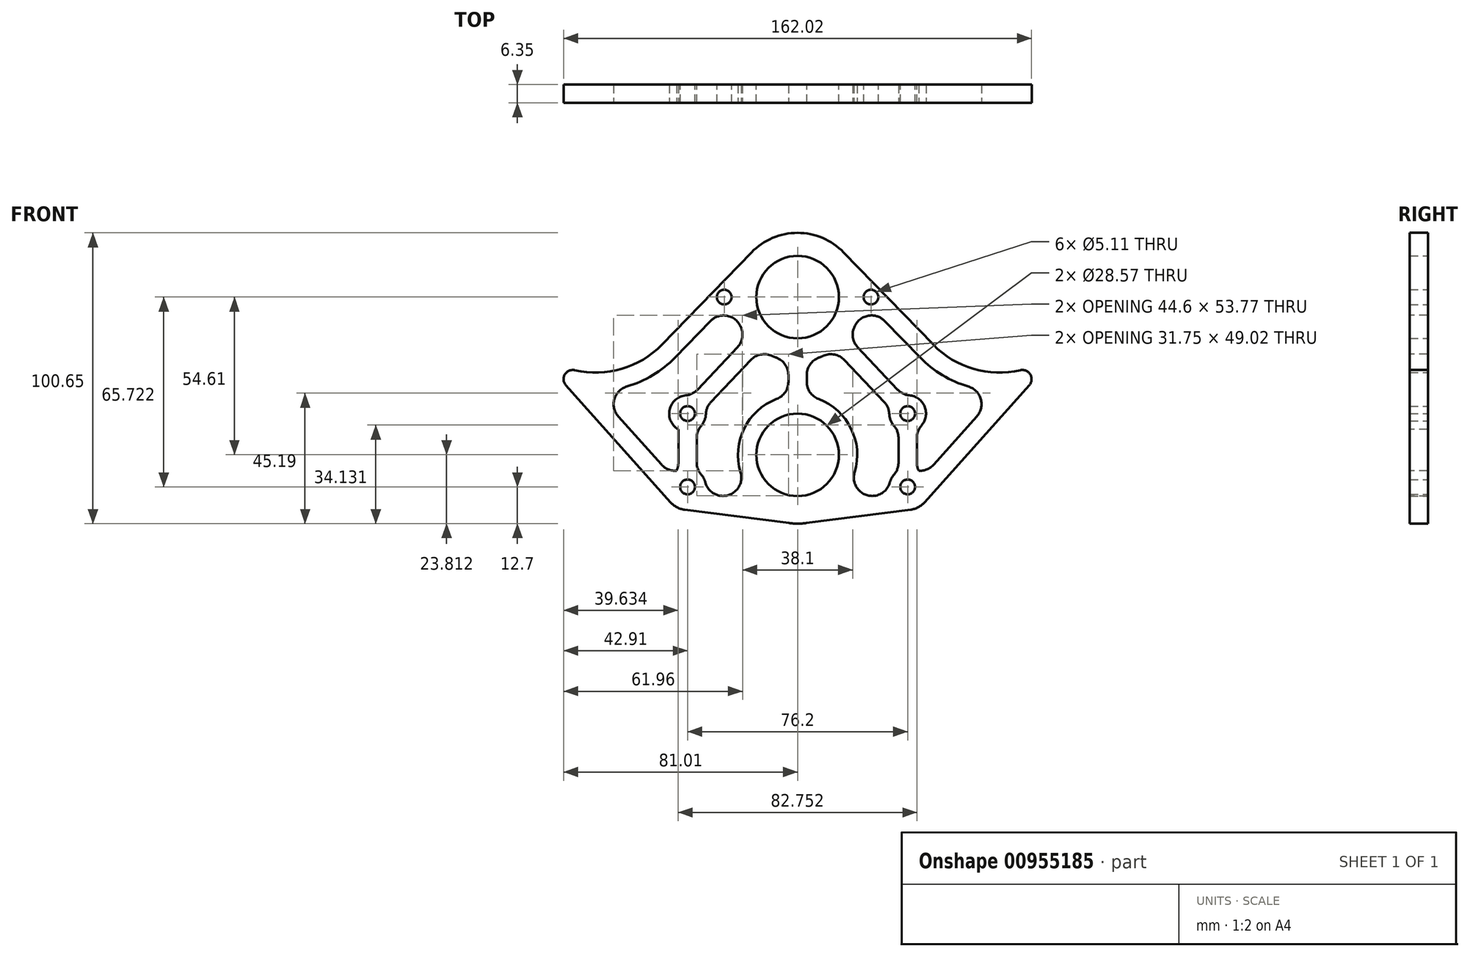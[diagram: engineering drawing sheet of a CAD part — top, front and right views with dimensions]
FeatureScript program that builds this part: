
annotation { "Feature Type Name" : "Feature", "Feature Type Description" : "" }
export const myFeature = defineFeature(function(context is Context, id is Id, definition is map)
    precondition{}
    {
        {
            var Q0;
            Q0=qCreatedBy(makeId("Front.planeOp"),FACE);
            var sketch = newSketch(context, id + "F0", { "sketchPlane" : qUnion([Q0])});
            skCircle(sketch, "E0", {"center": v(-69.85, 58.74) * mm, "radius": 31.88 * mm, "construction": true});
            skCircle(sketch, "E1", {"center": v(69.85, 58.74) * mm, "radius": 31.88 * mm, "construction": true});
            skLineSegment(sketch, "E2", {"start": v(-69.85, 58.74) * mm, "end": v(69.85, 58.74) * mm, "construction": true});
            skLineSegment(sketch, "E3", {"start": v(0, 58.74) * mm, "end": v(0, 0) * mm, "construction": true});
            skLineSegment(sketch, "E4.bottom", {"start": v(-101.6, -25.4) * mm, "end": v(101.6, -25.4) * mm, "construction": true});
            skLineSegment(sketch, "E4.top", {"start": v(-101.6, 25.4) * mm, "end": v(101.6, 25.4) * mm, "construction": true});
            skLineSegment(sketch, "E4.left", {"start": v(-101.6, -25.4) * mm, "end": v(-101.6, 25.4) * mm, "construction": true});
            skLineSegment(sketch, "E4.right", {"start": v(101.6, -25.4) * mm, "end": v(101.6, 25.4) * mm, "construction": true});
            skPoint(sketch, "E4.middle", {"position": v(0, 0) * mm});
            skCircle(sketch, "E5", {"center": v(0, -1.59) * mm, "radius": 50.8 * mm, "construction": true});
            skCircle(sketch, "E6", {"center": v(-69.85, 58.74) * mm, "radius": 7.62 * mm, "construction": true});
            skCircle(sketch, "E7", {"center": v(69.85, 58.74) * mm, "radius": 7.62 * mm, "construction": true});
            skCircle(sketch, "E8", {"center": v(0, 53.02) * mm, "radius": 38.1 * mm, "construction": true});
            skCircle(sketch, "E9", {"center": v(0, 53.02) * mm, "radius": 27.94 * mm, "construction": true});
            skCircle(sketch, "E10", {"center": v(0, -1.59) * mm, "radius": 26.67 * mm, "construction": true});
            skCircle(sketch, "E11", {"center": v(0, 53.02) * mm, "radius": 19.05 * mm, "construction": true});
            skCircle(sketch, "E12", {"center": v(0, -1.59) * mm, "radius": 35.56 * mm, "construction": true});
            skCircle(sketch, "E13", {"center": v(-69.85, 58.74) * mm, "radius": 8.9 * mm, "construction": true});
            skCircle(sketch, "E14", {"center": v(69.85, 58.74) * mm, "radius": 8.9 * mm, "construction": true});
            skCircle(sketch, "E15", {"center": v(0, 53.02) * mm, "radius": 14.29 * mm});
            skCircle(sketch, "E16", {"center": v(0, -1.59) * mm, "radius": 14.29 * mm});
            skCircle(sketch, "E17", {"center": v(-88.9, 12.7) * mm, "radius": 2.55 * mm, "construction": true});
            skCircle(sketch, "E18.0.1.0", {"center": v(-88.9, -12.7) * mm, "radius": 2.55 * mm, "construction": true});
            skCircle(sketch, "E18.1.0.0", {"center": v(-63.5, 12.7) * mm, "radius": 2.55 * mm, "construction": true});
            skCircle(sketch, "E18.1.1.0", {"center": v(-63.5, -12.7) * mm, "radius": 2.55 * mm, "construction": true});
            skCircle(sketch, "E18.2.0.0", {"center": v(-38.1, 12.7) * mm, "radius": 2.55 * mm});
            skCircle(sketch, "E18.2.1.0", {"center": v(-38.1, -12.7) * mm, "radius": 2.55 * mm});
            skCircle(sketch, "E18.3.0.0", {"center": v(-12.7, 12.7) * mm, "radius": 2.55 * mm, "construction": true});
            skCircle(sketch, "E18.3.1.0", {"center": v(-12.7, -12.7) * mm, "radius": 2.55 * mm, "construction": true});
            skCircle(sketch, "E18.4.0.0", {"center": v(12.7, 12.7) * mm, "radius": 2.55 * mm, "construction": true});
            skCircle(sketch, "E18.4.1.0", {"center": v(12.7, -12.7) * mm, "radius": 2.55 * mm, "construction": true});
            skCircle(sketch, "E18.5.0.0", {"center": v(38.1, 12.7) * mm, "radius": 2.55 * mm});
            skCircle(sketch, "E18.5.1.0", {"center": v(38.1, -12.7) * mm, "radius": 2.55 * mm});
            skCircle(sketch, "E18.6.0.0", {"center": v(63.5, 12.7) * mm, "radius": 2.55 * mm, "construction": true});
            skCircle(sketch, "E18.6.1.0", {"center": v(63.5, -12.7) * mm, "radius": 2.55 * mm, "construction": true});
            skCircle(sketch, "E18.7.0.0", {"center": v(88.9, 12.7) * mm, "radius": 2.55 * mm, "construction": true});
            skCircle(sketch, "E18.7.1.0", {"center": v(88.9, -12.7) * mm, "radius": 2.55 * mm, "construction": true});
            skLineSegment(sketch, "E18.direction1", {"start": v(-88.9, 12.7) * mm, "end": v(-63.5, 12.7) * mm, "construction": true});
            skLineSegment(sketch, "E18.direction2", {"start": v(-88.9, 12.7) * mm, "end": v(-88.9, -12.7) * mm, "construction": true});
            skArc(sketch, "E19", {"start": v(-93.62, 37.5) * mm, "mid": v(-98.95, 71.76) * mm, "end": v(-69.85, 90.61) * mm, "construction": true});
            skLineSegment(sketch, "E20", {"start": v(-69.85, 90.61) * mm, "end": v(69.85, 90.61) * mm, "construction": true});
            skArc(sketch, "E21", {"start": v(69.85, 90.61) * mm, "mid": v(98.95, 71.76) * mm, "end": v(93.62, 37.5) * mm, "construction": true});
            skCircle(sketch, "E22", {"center": v(-69.85, 58.74) * mm, "radius": 9.55 * mm, "construction": true});
            skCircle(sketch, "E23", {"center": v(69.85, 58.74) * mm, "radius": 9.55 * mm, "construction": true});
            skLineSegment(sketch, "E24", {"start": v(-67.64, 84.04) * mm, "end": v(-69.85, 58.74) * mm, "construction": true});
            skLineSegment(sketch, "E25", {"start": v(-69.85, 58.74) * mm, "end": v(-72.06, 33.43) * mm, "construction": true});
            skCircle(sketch, "E26", {"center": v(-72.06, 33.43) * mm, "radius": 2.55 * mm, "construction": true});
            skCircle(sketch, "E27", {"center": v(-67.64, 84.04) * mm, "radius": 2.55 * mm, "construction": true});
            skCircle(sketch, "E28.MirrorC", {"center": v(72.06, 33.43) * mm, "radius": 2.55 * mm, "construction": true});
            skLineSegment(sketch, "E29.MirrorCS", {"start": v(69.85, 58.74) * mm, "end": v(72.06, 33.43) * mm, "construction": true});
            skLineSegment(sketch, "E30.MirrorCS", {"start": v(67.64, 84.04) * mm, "end": v(69.85, 58.74) * mm, "construction": true});
            skCircle(sketch, "E31.MirrorC", {"center": v(67.64, 84.04) * mm, "radius": 2.55 * mm, "construction": true});
            skCircle(sketch, "E32", {"center": v(0, -1.59) * mm, "radius": 23.81 * mm, "construction": true});
            skArc(sketch, "E33", {"start": v(3.03, -25.2) * mm, "mid": v(0, -25.4) * mm, "end": v(-3.03, -25.2) * mm});
            skCircle(sketch, "E34", {"center": v(-38.1, -12.7) * mm, "radius": 7.94 * mm, "construction": true});
            skCircle(sketch, "E35", {"center": v(38.1, -12.7) * mm, "radius": 7.94 * mm, "construction": true});
            skLineSegment(sketch, "E36", {"start": v(-3.03, -25.2) * mm, "end": v(-39.11, -20.57) * mm});
            skArc(sketch, "E37", {"start": v(-39.11, -20.57) * mm, "mid": v(-41.8, -19.72) * mm, "end": v(-44.02, -18) * mm});
            skLineSegment(sketch, "E38", {"start": v(-44.02, -18) * mm, "end": v(-80.2, 22.5) * mm});
            skLineSegment(sketch, "E39", {"start": v(3.03, -25.2) * mm, "end": v(39.11, -20.57) * mm});
            skArc(sketch, "E40", {"start": v(39.11, -20.57) * mm, "mid": v(41.8, -19.72) * mm, "end": v(44.02, -18) * mm});
            skLineSegment(sketch, "E41", {"start": v(44.02, -18) * mm, "end": v(80.2, 22.5) * mm});
            skCircle(sketch, "E42", {"center": v(-51.03, 75.8) * mm, "radius": 17.78 * mm, "construction": true});
            skCircle(sketch, "E43", {"center": v(-53.69, 37.52) * mm, "radius": 17.78 * mm, "construction": true});
            skCircle(sketch, "E44", {"center": v(51.03, 75.8) * mm, "radius": 17.78 * mm, "construction": true});
            skCircle(sketch, "E45", {"center": v(53.69, 37.52) * mm, "radius": 17.78 * mm, "construction": true});
            skCircle(sketch, "E46", {"center": v(-51.03, 75.8) * mm, "radius": 11.11 * mm, "construction": true});
            skCircle(sketch, "E47", {"center": v(-53.69, 37.52) * mm, "radius": 11.11 * mm, "construction": true});
            skCircle(sketch, "E48", {"center": v(53.69, 37.52) * mm, "radius": 11.11 * mm, "construction": true});
            skCircle(sketch, "E49", {"center": v(51.03, 75.8) * mm, "radius": 11.11 * mm, "construction": true});
            skCircle(sketch, "E50", {"center": v(0, 53.02) * mm, "radius": 22.23 * mm, "construction": true});
            skArc(sketch, "E51", {"start": v(-77.12, 27.7) * mm, "mid": v(-60.88, 28.15) * mm, "end": v(-46.98, 36.54) * mm});
            skLineSegment(sketch, "E52", {"start": v(-46.98, 36.54) * mm, "end": v(-15.95, 68.5) * mm});
            skArc(sketch, "E53", {"start": v(15.95, 68.5) * mm, "mid": v(0, 75.25) * mm, "end": v(-15.95, 68.5) * mm});
            skArc(sketch, "E54", {"start": v(46.98, 36.54) * mm, "mid": v(60.88, 28.15) * mm, "end": v(77.12, 27.7) * mm});
            skLineSegment(sketch, "E55", {"start": v(46.98, 36.54) * mm, "end": v(15.95, 68.5) * mm});
            skPoint(sketch, "E56.visualSharp", {"position": v(-93.62, 37.5) * mm});
            skArc(sketch, "E56.filletArc", {"start": v(-77.12, 27.7) * mm, "mid": v(-80.57, 26.23) * mm, "end": v(-80.2, 22.5) * mm});
            skPoint(sketch, "E57.visualSharp", {"position": v(93.62, 37.5) * mm});
            skArc(sketch, "E57.filletArc", {"start": v(80.2, 22.5) * mm, "mid": v(80.57, 26.23) * mm, "end": v(77.12, 27.7) * mm});
            skLineSegment(sketch, "E58", {"start": v(25.4, 53.02) * mm, "end": v(0, 53.02) * mm, "construction": true});
            skLineSegment(sketch, "E59", {"start": v(0, 53.02) * mm, "end": v(-25.4, 53.02) * mm, "construction": true});
            skCircle(sketch, "E60", {"center": v(-25.4, 53.02) * mm, "radius": 2.55 * mm});
            skCircle(sketch, "E61", {"center": v(25.4, 53.02) * mm, "radius": 2.55 * mm});
            skSolve(sketch);
        }
        {
            var Q0;
            Q0=qSketchRegion(id+"F0",true);
            extrude(context, id + "F1", {"entities" : qUnion([Q0]), "depth" : 6.35 * mm, "offsetDistance" : 25.4 * mm});
        }
        {
            var Q0;
            Q0=makeQuery(id+"F1.opExtrude","CAP_FACE",FACE,{"disambiguationData":[OSD([sQuery(id+"F0.wireOp",EDGE,"E15"),sQuery(id+"F0.wireOp",EDGE,"E16"),sQuery(id+"F0.wireOp",EDGE,"E18.2.0.0"),sQuery(id+"F0.wireOp",EDGE,"E18.2.1.0"),sQuery(id+"F0.wireOp",EDGE,"E18.5.0.0"),sQuery(id+"F0.wireOp",EDGE,"E18.5.1.0"),sQuery(id+"F0.wireOp",EDGE,"E33"),sQuery(id+"F0.wireOp",EDGE,"E36"),sQuery(id+"F0.wireOp",EDGE,"E37"),sQuery(id+"F0.wireOp",EDGE,"E38"),sQuery(id+"F0.wireOp",EDGE,"E39"),sQuery(id+"F0.wireOp",EDGE,"E40"),sQuery(id+"F0.wireOp",EDGE,"E41"),sQuery(id+"F0.wireOp",EDGE,"E51"),sQuery(id+"F0.wireOp",EDGE,"E52"),sQuery(id+"F0.wireOp",EDGE,"E53"),sQuery(id+"F0.wireOp",EDGE,"E54"),sQuery(id+"F0.wireOp",EDGE,"E55"),sQuery(id+"F0.wireOp",EDGE,"E56.filletArc"),sQuery(id+"F0.wireOp",EDGE,"E57.filletArc"),sQuery(id+"F0.wireOp",EDGE,"E60"),sQuery(id+"F0.wireOp",EDGE,"E61")])],"isStart":false});
            var sketch = newSketch(context, id + "F2", { "sketchPlane" : qUnion([Q0])});
            skCircle(sketch, "E62", {"center": v(0, 53.02) * mm, "radius": 22.23 * mm, "construction": true});
            skCircle(sketch, "E63", {"center": v(25.4, 53.02) * mm, "radius": 6.35 * mm, "construction": true});
            skCircle(sketch, "E64", {"center": v(-25.4, 53.02) * mm, "radius": 6.35 * mm, "construction": true});
            skCircle(sketch, "E65", {"center": v(-38.1, 12.7) * mm, "radius": 6.35 * mm, "construction": true});
            skCircle(sketch, "E66", {"center": v(-38.1, -12.7) * mm, "radius": 6.35 * mm, "construction": true});
            skCircle(sketch, "E67", {"center": v(38.1, -12.7) * mm, "radius": 6.35 * mm, "construction": true});
            skCircle(sketch, "E68", {"center": v(38.1, 12.7) * mm, "radius": 6.35 * mm, "construction": true});
            skLineSegment(sketch, "E69", {"start": v(-38.1, -12.7) * mm, "end": v(-38.1, 12.7) * mm, "construction": true});
            skLineSegment(sketch, "E70", {"start": v(-41.27, -7.2) * mm, "end": v(-41.27, 7.2) * mm});
            skLineSegment(sketch, "E71", {"start": v(-34.92, -7.2) * mm, "end": v(-34.92, 7.2) * mm});
            skCircle(sketch, "E72", {"center": v(0, -1.59) * mm, "radius": 20.64 * mm, "construction": true});
            skLineSegment(sketch, "E73", {"start": v(0, -1.59) * mm, "end": v(0, 53.02) * mm, "construction": true});
            skLineSegment(sketch, "E74", {"start": v(-3.18, 18.8) * mm, "end": v(-3.18, 31.03) * mm});
            skLineSegment(sketch, "E75", {"start": v(0, 53.02) * mm, "end": v(-38.1, 12.7) * mm, "construction": true});
            skLineSegment(sketch, "E76", {"start": v(-32.02, 14.52) * mm, "end": v(-12.8, 34.85) * mm});
            skArc(sketch, "E77.0", {"start": v(-38.3, -14.27) * mm, "mid": v(-38.84, -14.1) * mm, "end": v(-39.28, -13.76) * mm, "construction": true});
            skLineSegment(sketch, "E77.1", {"start": v(42.42, 32.11) * mm, "end": v(11.4, 64.08) * mm, "construction": true});
            skArc(sketch, "E77.2", {"start": v(11.4, 64.08) * mm, "mid": v(0, 68.9) * mm, "end": v(-11.4, 64.08) * mm, "construction": true});
            skLineSegment(sketch, "E77.3", {"start": v(-42.42, 32.11) * mm, "end": v(-11.4, 64.08) * mm, "construction": true});
            skArc(sketch, "E77.4", {"start": v(-69.92, 20.51) * mm, "mid": v(-54.99, 23.52) * mm, "end": v(-42.42, 32.11) * mm});
            skArc(sketch, "E77.5", {"start": v(42.42, 32.11) * mm, "mid": v(54.99, 23.52) * mm, "end": v(69.92, 20.51) * mm, "construction": true});
            skLineSegment(sketch, "E77.6", {"start": v(-39.28, -13.76) * mm, "end": v(-69.92, 20.51) * mm, "construction": true});
            skLineSegment(sketch, "E77.7", {"start": v(39.28, -13.76) * mm, "end": v(69.92, 20.51) * mm, "construction": true});
            skArc(sketch, "E77.8", {"start": v(38.3, -14.27) * mm, "mid": v(38.84, -14.1) * mm, "end": v(39.28, -13.76) * mm, "construction": true});
            skLineSegment(sketch, "E77.9", {"start": v(2.22, -18.9) * mm, "end": v(38.3, -14.27) * mm, "construction": true});
            skArc(sketch, "E77.10", {"start": v(2.22, -18.9) * mm, "mid": v(0, -19.05) * mm, "end": v(-2.22, -18.9) * mm, "construction": true});
            skLineSegment(sketch, "E77.11", {"start": v(-2.22, -18.9) * mm, "end": v(-38.3, -14.27) * mm, "construction": true});
            skArc(sketch, "E78", {"start": v(-32.2, -15.06) * mm, "mid": v(-32.1, -10.62) * mm, "end": v(-34.92, -7.2) * mm});
            skArc(sketch, "E79", {"start": v(-3.18, 18.8) * mm, "mid": v(-19.9, 3.87) * mm, "end": v(-13.13, -17.5) * mm});
            skLineSegment(sketch, "E80", {"start": v(-13.13, -17.5) * mm, "end": v(-32.2, -15.06) * mm});
            skArc(sketch, "E81", {"start": v(-32.02, 14.52) * mm, "mid": v(-32.2, 10.35) * mm, "end": v(-34.92, 7.2) * mm});
            skArc(sketch, "E82", {"start": v(-12.8, 34.85) * mm, "mid": v(-8.21, 32.37) * mm, "end": v(-3.17, 31.03) * mm});
            skLineSegment(sketch, "E83", {"start": v(-36.63, 18.88) * mm, "end": v(-17.42, 39.21) * mm});
            skArc(sketch, "E84", {"start": v(-41.27, 7.2) * mm, "mid": v(-44, 15.05) * mm, "end": v(-36.63, 18.88) * mm});
            skArc(sketch, "E85", {"start": v(-17.42, 39.21) * mm, "mid": v(-20, 43.33) * mm, "end": v(-21.63, 47.91) * mm});
            skArc(sketch, "E86", {"start": v(-27.82, 47.15) * mm, "mid": v(-24.63, 46.72) * mm, "end": v(-21.63, 47.91) * mm});
            skLineSegment(sketch, "E87", {"start": v(-42.42, 32.11) * mm, "end": v(-27.82, 47.15) * mm});
            skLineSegment(sketch, "E88", {"start": v(-43.38, -9.17) * mm, "end": v(-69.92, 20.51) * mm});
            skArc(sketch, "E89", {"start": v(-41.27, -7.2) * mm, "mid": v(-42.44, -8.07) * mm, "end": v(-43.38, -9.17) * mm});
            skArc(sketch, "E90.MirrorCS", {"start": v(41.27, -7.2) * mm, "mid": v(42.44, -8.07) * mm, "end": v(43.38, -9.17) * mm});
            skArc(sketch, "E91.MirrorCS", {"start": v(27.82, 47.15) * mm, "mid": v(24.63, 46.72) * mm, "end": v(21.63, 47.91) * mm});
            skArc(sketch, "E92.MirrorCS", {"start": v(32.2, -15.06) * mm, "mid": v(32.1, -10.62) * mm, "end": v(34.92, -7.2) * mm});
            skLineSegment(sketch, "E93.MirrorCS", {"start": v(13.13, -17.5) * mm, "end": v(32.2, -15.06) * mm});
            skLineSegment(sketch, "E94.MirrorCS", {"start": v(43.38, -9.17) * mm, "end": v(69.92, 20.51) * mm});
            skArc(sketch, "E95.MirrorCS", {"start": v(41.27, 7.2) * mm, "mid": v(44, 15.05) * mm, "end": v(36.63, 18.88) * mm});
            skArc(sketch, "E96.MirrorCS", {"start": v(32.02, 14.52) * mm, "mid": v(32.2, 10.35) * mm, "end": v(34.92, 7.2) * mm});
            skLineSegment(sketch, "E97.MirrorCS", {"start": v(42.42, 32.11) * mm, "end": v(27.82, 47.15) * mm});
            skLineSegment(sketch, "E98.MirrorCS", {"start": v(32.02, 14.52) * mm, "end": v(12.8, 34.85) * mm});
            skLineSegment(sketch, "E99.MirrorCS", {"start": v(3.18, 18.8) * mm, "end": v(3.18, 31.03) * mm});
            skArc(sketch, "E100.MirrorCS", {"start": v(69.92, 20.51) * mm, "mid": v(54.99, 23.52) * mm, "end": v(42.42, 32.11) * mm});
            skLineSegment(sketch, "E101.MirrorCS", {"start": v(41.27, -7.2) * mm, "end": v(41.27, 7.2) * mm});
            skLineSegment(sketch, "E102.MirrorCS", {"start": v(0, 53.02) * mm, "end": v(38.1, 12.7) * mm, "construction": true});
            skLineSegment(sketch, "E103.MirrorCS", {"start": v(34.92, -7.2) * mm, "end": v(34.92, 7.2) * mm});
            skArc(sketch, "E104.MirrorCS", {"start": v(17.42, 39.21) * mm, "mid": v(20, 43.33) * mm, "end": v(21.63, 47.91) * mm});
            skArc(sketch, "E105.MirrorCS", {"start": v(-2.22, -18.9) * mm, "mid": v(0, -19.05) * mm, "end": v(2.22, -18.9) * mm, "construction": true});
            skArc(sketch, "E106.MirrorCS", {"start": v(3.18, 18.8) * mm, "mid": v(19.9, 3.87) * mm, "end": v(13.13, -17.5) * mm});
            skLineSegment(sketch, "E107.MirrorCS", {"start": v(38.1, -12.7) * mm, "end": v(38.1, 12.7) * mm, "construction": true});
            skArc(sketch, "E108.MirrorCS", {"start": v(12.8, 34.85) * mm, "mid": v(8.21, 32.37) * mm, "end": v(3.17, 31.03) * mm});
            skLineSegment(sketch, "E109.MirrorCS", {"start": v(36.63, 18.88) * mm, "end": v(17.42, 39.21) * mm});
            skSolve(sketch);
        }
        {
            var Q0;
            Q0=qSketchRegion(id+"F2",true);
            extrude(context, id + "F3", {"entities" : qUnion([Q0]), "operationType" : NewBodyOperationType.REMOVE, "oppositeDirection" : true, "depth" : 25.4 * mm, "offsetDistance" : 25.4 * mm});
        }
        {
            var Q0;
            Q0=makeQuery(id+"F3.boolean.opBoolean","COPY",EDGE,{"derivedFrom":makeQuery(id+"F3.opExtrude","SWEPT_EDGE",EDGE,{"disambiguationData":[OSD([sQuery(id+"F2.wireOp",EDGE,"E86"),sQuery(id+"F2.wireOp",EDGE,"E87")])]})});
            var Q1;
            Q1=makeQuery(id+"F3.boolean.opBoolean","COPY",EDGE,{"derivedFrom":makeQuery(id+"F3.opExtrude","SWEPT_EDGE",EDGE,{"disambiguationData":[OSD([sQuery(id+"F2.wireOp",EDGE,"E85"),sQuery(id+"F2.wireOp",EDGE,"E86")])]})});
            var Q2;
            Q2=makeQuery(id+"F3.boolean.opBoolean","COPY",EDGE,{"derivedFrom":makeQuery(id+"F3.opExtrude","SWEPT_EDGE",EDGE,{"disambiguationData":[OSD([sQuery(id+"F2.wireOp",EDGE,"E83"),sQuery(id+"F2.wireOp",EDGE,"E85")])]})});
            var Q3;
            Q3=makeQuery(id+"F3.boolean.opBoolean","COPY",EDGE,{"derivedFrom":makeQuery(id+"F3.opExtrude","SWEPT_EDGE",EDGE,{"disambiguationData":[OSD([sQuery(id+"F2.wireOp",EDGE,"E74"),sQuery(id+"F2.wireOp",EDGE,"E79")])]})});
            var Q4;
            Q4=makeQuery(id+"F3.boolean.opBoolean","COPY",EDGE,{"derivedFrom":makeQuery(id+"F3.opExtrude","SWEPT_EDGE",EDGE,{"disambiguationData":[OSD([sQuery(id+"F2.wireOp",EDGE,"E83"),sQuery(id+"F2.wireOp",EDGE,"E84")])]})});
            var Q5;
            Q5=makeQuery(id+"F3.boolean.opBoolean","COPY",EDGE,{"derivedFrom":makeQuery(id+"F3.opExtrude","SWEPT_EDGE",EDGE,{"disambiguationData":[OSD([sQuery(id+"F2.wireOp",EDGE,"E70"),sQuery(id+"F2.wireOp",EDGE,"E89")])]})});
            var Q6;
            Q6=makeQuery(id+"F3.boolean.opBoolean","COPY",EDGE,{"derivedFrom":makeQuery(id+"F3.opExtrude","SWEPT_EDGE",EDGE,{"disambiguationData":[OSD([sQuery(id+"F2.wireOp",EDGE,"E88"),sQuery(id+"F2.wireOp",EDGE,"E89")])]})});
            var Q7;
            Q7=makeQuery(id+"F3.boolean.opBoolean","COPY",EDGE,{"derivedFrom":makeQuery(id+"F3.opExtrude","SWEPT_EDGE",EDGE,{"disambiguationData":[OSD([sQuery(id+"F2.wireOp",EDGE,"E77.4"),sQuery(id+"F2.wireOp",EDGE,"E88")])]})});
            var Q8;
            Q8=makeQuery(id+"F3.boolean.opBoolean","COPY",EDGE,{"derivedFrom":makeQuery(id+"F3.opExtrude","SWEPT_EDGE",EDGE,{"disambiguationData":[OSD([sQuery(id+"F2.wireOp",EDGE,"E71"),sQuery(id+"F2.wireOp",EDGE,"E78")])]})});
            var Q9;
            Q9=makeQuery(id+"F3.boolean.opBoolean","COPY",EDGE,{"derivedFrom":makeQuery(id+"F3.opExtrude","SWEPT_EDGE",EDGE,{"disambiguationData":[OSD([sQuery(id+"F2.wireOp",EDGE,"E71"),sQuery(id+"F2.wireOp",EDGE,"E81")])]})});
            var Q10;
            Q10=makeQuery(id+"F3.boolean.opBoolean","COPY",EDGE,{"derivedFrom":makeQuery(id+"F3.opExtrude","SWEPT_EDGE",EDGE,{"disambiguationData":[OSD([sQuery(id+"F2.wireOp",EDGE,"E76"),sQuery(id+"F2.wireOp",EDGE,"E81")])]})});
            var Q11;
            Q11=makeQuery(id+"F3.boolean.opBoolean","COPY",EDGE,{"derivedFrom":makeQuery(id+"F3.opExtrude","SWEPT_EDGE",EDGE,{"disambiguationData":[OSD([sQuery(id+"F2.wireOp",EDGE,"E78"),sQuery(id+"F2.wireOp",EDGE,"E80")])]})});
            var Q12;
            Q12=makeQuery(id+"F3.boolean.opBoolean","COPY",EDGE,{"derivedFrom":makeQuery(id+"F3.opExtrude","SWEPT_EDGE",EDGE,{"disambiguationData":[OSD([sQuery(id+"F2.wireOp",EDGE,"E99.MirrorCS"),sQuery(id+"F2.wireOp",EDGE,"E106.MirrorCS")])]})});
            var Q13;
            Q13=makeQuery(id+"F3.boolean.opBoolean","COPY",EDGE,{"derivedFrom":makeQuery(id+"F3.opExtrude","SWEPT_EDGE",EDGE,{"disambiguationData":[OSD([sQuery(id+"F2.wireOp",EDGE,"E79"),sQuery(id+"F2.wireOp",EDGE,"E80")])]})});
            var Q14;
            Q14=makeQuery(id+"F3.boolean.opBoolean","COPY",EDGE,{"derivedFrom":makeQuery(id+"F3.opExtrude","SWEPT_EDGE",EDGE,{"disambiguationData":[OSD([sQuery(id+"F2.wireOp",EDGE,"E92.MirrorCS"),sQuery(id+"F2.wireOp",EDGE,"E93.MirrorCS")])]})});
            var Q15;
            Q15=makeQuery(id+"F3.boolean.opBoolean","COPY",EDGE,{"derivedFrom":makeQuery(id+"F3.opExtrude","SWEPT_EDGE",EDGE,{"disambiguationData":[OSD([sQuery(id+"F2.wireOp",EDGE,"E92.MirrorCS"),sQuery(id+"F2.wireOp",EDGE,"E103.MirrorCS")])]})});
            var Q16;
            Q16=makeQuery(id+"F3.boolean.opBoolean","COPY",EDGE,{"derivedFrom":makeQuery(id+"F3.opExtrude","SWEPT_EDGE",EDGE,{"disambiguationData":[OSD([sQuery(id+"F2.wireOp",EDGE,"E93.MirrorCS"),sQuery(id+"F2.wireOp",EDGE,"E106.MirrorCS")])]})});
            var Q17;
            Q17=makeQuery(id+"F3.boolean.opBoolean","COPY",EDGE,{"derivedFrom":makeQuery(id+"F3.opExtrude","SWEPT_EDGE",EDGE,{"disambiguationData":[OSD([sQuery(id+"F2.wireOp",EDGE,"E95.MirrorCS"),sQuery(id+"F2.wireOp",EDGE,"E109.MirrorCS")])]})});
            var Q18;
            Q18=makeQuery(id+"F3.boolean.opBoolean","COPY",EDGE,{"derivedFrom":makeQuery(id+"F3.opExtrude","SWEPT_EDGE",EDGE,{"disambiguationData":[OSD([sQuery(id+"F2.wireOp",EDGE,"E95.MirrorCS"),sQuery(id+"F2.wireOp",EDGE,"E101.MirrorCS")])]})});
            var Q19;
            Q19=makeQuery(id+"F3.boolean.opBoolean","COPY",EDGE,{"derivedFrom":makeQuery(id+"F3.opExtrude","SWEPT_EDGE",EDGE,{"disambiguationData":[OSD([sQuery(id+"F2.wireOp",EDGE,"E104.MirrorCS"),sQuery(id+"F2.wireOp",EDGE,"E109.MirrorCS")])]})});
            var Q20;
            Q20=makeQuery(id+"F3.boolean.opBoolean","COPY",EDGE,{"derivedFrom":makeQuery(id+"F3.opExtrude","SWEPT_EDGE",EDGE,{"disambiguationData":[OSD([sQuery(id+"F2.wireOp",EDGE,"E76"),sQuery(id+"F2.wireOp",EDGE,"E82")])]})});
            var Q21;
            Q21=makeQuery(id+"F3.boolean.opBoolean","COPY",EDGE,{"derivedFrom":makeQuery(id+"F3.opExtrude","SWEPT_EDGE",EDGE,{"disambiguationData":[OSD([sQuery(id+"F2.wireOp",EDGE,"E99.MirrorCS"),sQuery(id+"F2.wireOp",EDGE,"E108.MirrorCS")])]})});
            var Q22;
            Q22=makeQuery(id+"F3.boolean.opBoolean","COPY",EDGE,{"derivedFrom":makeQuery(id+"F3.opExtrude","SWEPT_EDGE",EDGE,{"disambiguationData":[OSD([sQuery(id+"F2.wireOp",EDGE,"E74"),sQuery(id+"F2.wireOp",EDGE,"E82")])]})});
            var Q23;
            Q23=makeQuery(id+"F3.boolean.opBoolean","COPY",EDGE,{"derivedFrom":makeQuery(id+"F3.opExtrude","SWEPT_EDGE",EDGE,{"disambiguationData":[OSD([sQuery(id+"F2.wireOp",EDGE,"E98.MirrorCS"),sQuery(id+"F2.wireOp",EDGE,"E108.MirrorCS")])]})});
            var Q24;
            Q24=makeQuery(id+"F3.boolean.opBoolean","COPY",EDGE,{"derivedFrom":makeQuery(id+"F3.opExtrude","SWEPT_EDGE",EDGE,{"disambiguationData":[OSD([sQuery(id+"F2.wireOp",EDGE,"E96.MirrorCS"),sQuery(id+"F2.wireOp",EDGE,"E98.MirrorCS")])]})});
            var Q25;
            Q25=makeQuery(id+"F3.boolean.opBoolean","COPY",EDGE,{"derivedFrom":makeQuery(id+"F3.opExtrude","SWEPT_EDGE",EDGE,{"disambiguationData":[OSD([sQuery(id+"F2.wireOp",EDGE,"E96.MirrorCS"),sQuery(id+"F2.wireOp",EDGE,"E103.MirrorCS")])]})});
            var Q26;
            Q26=makeQuery(id+"F3.boolean.opBoolean","COPY",EDGE,{"derivedFrom":makeQuery(id+"F3.opExtrude","SWEPT_EDGE",EDGE,{"disambiguationData":[OSD([sQuery(id+"F2.wireOp",EDGE,"E94.MirrorCS"),sQuery(id+"F2.wireOp",EDGE,"E100.MirrorCS")])]})});
            var Q27;
            Q27=makeQuery(id+"F3.boolean.opBoolean","COPY",EDGE,{"derivedFrom":makeQuery(id+"F3.opExtrude","SWEPT_EDGE",EDGE,{"disambiguationData":[OSD([sQuery(id+"F2.wireOp",EDGE,"E91.MirrorCS"),sQuery(id+"F2.wireOp",EDGE,"E104.MirrorCS")])]})});
            var Q28;
            Q28=makeQuery(id+"F3.boolean.opBoolean","COPY",EDGE,{"derivedFrom":makeQuery(id+"F3.opExtrude","SWEPT_EDGE",EDGE,{"disambiguationData":[OSD([sQuery(id+"F2.wireOp",EDGE,"E91.MirrorCS"),sQuery(id+"F2.wireOp",EDGE,"E97.MirrorCS")])]})});
            var Q29;
            Q29=makeQuery(id+"F3.boolean.opBoolean","COPY",EDGE,{"derivedFrom":makeQuery(id+"F3.opExtrude","SWEPT_EDGE",EDGE,{"disambiguationData":[OSD([sQuery(id+"F2.wireOp",EDGE,"E90.MirrorCS"),sQuery(id+"F2.wireOp",EDGE,"E101.MirrorCS")])]})});
            var Q30;
            Q30=makeQuery(id+"F3.boolean.opBoolean","COPY",EDGE,{"derivedFrom":makeQuery(id+"F3.opExtrude","SWEPT_EDGE",EDGE,{"disambiguationData":[OSD([sQuery(id+"F2.wireOp",EDGE,"E90.MirrorCS"),sQuery(id+"F2.wireOp",EDGE,"E94.MirrorCS")])]})});
            fillet(context, id + "F4", {"entities" : qUnion([Q0, Q1, Q2, Q3, Q4, Q5, Q6, Q7, Q8, Q9, Q10, Q11, Q12, Q13, Q14, Q15, Q16, Q17, Q18, Q19, Q20, Q21, Q22, Q23, Q24, Q25, Q26, Q27, Q28, Q29, Q30]), "radius" : 6.35 * mm, "tangentPropagation" : true, "allowEdgeOverflow" : false});
        }
    });
